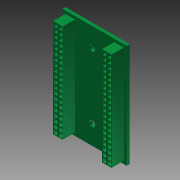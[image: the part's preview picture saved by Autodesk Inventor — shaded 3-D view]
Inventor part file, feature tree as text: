
AUTODESK INVENTOR PART (.ipt)
format: ipt  version: 2012 (Build 160160000, 160)  size: 452,608 bytes
history: native  units: in
note: dims shown in document units (in); Inventor stores cm internally (conversion verified against a paired STEP export)
features: extrude x2, sketch x1
ambient origin geometry x8: Origin, YZ Plane, XZ Plane, XY Plane, X Axis, Y Axis, Z Axis, Center Point
bodies: Solid1 (feature_tree)
feature tree (3):
  sketch  "Sketch1"  dims[d3=2.0069in d4=0.1969in d5=0.0591in d6=0.0591in d7=0.0669in d8=0.0669in d9=0.1in d10=0.0669in d11=0.0669in d12=0.0197in d13=0.0197in d14=0.0197in d15=0.0669in d16=0.0669in d17=0.1in d18=0.0669in d19=0.0669in d21=0.1in d22=0.1in d23=0.0197in d24=3.937in d26=0.2in d27=0.3937in d29=1.0in d31=0.7874in d33=1.0in d34=0.3937in d36=1.0in d38=0.0591in d39=0.0591in d40=0.6075in d41=0.6075in d42=0.3937in d43=0.3937in d44=0.1181in d45=0.1181in d46=0.063in d47=0.0in d48=0.315in d49=0.0in]
  extrude  "Extrusion1"  Depth=0.1969in
  extrude  "Extrusion2"  Depth=0.0591in
